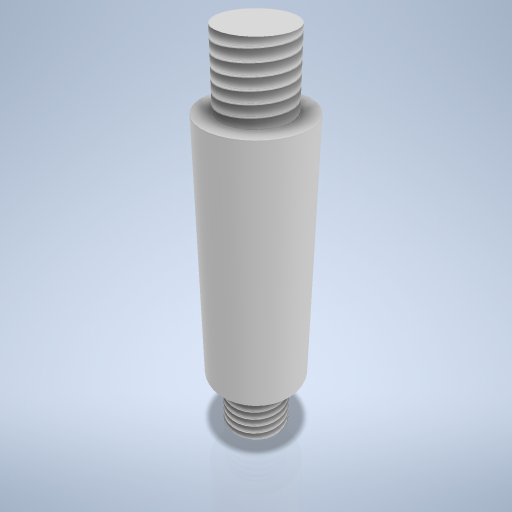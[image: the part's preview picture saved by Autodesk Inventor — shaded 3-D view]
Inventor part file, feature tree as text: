
AUTODESK INVENTOR PART (.ipt)
format: ipt  version: 2024.2 (Build 282272000, 272)  size: 269,824 bytes
history: native  units: mm
features: revolve x1, thread x1, sketch x1
ambient origin geometry x8: Origin, YZ Plane, XZ Plane, XY Plane, X Axis, Y Axis, Z Axis, Center Point
bodies: Volumenkörper1 (feature_tree)
feature tree (3):
  revolve  "Umdrehung1"
  thread  "Gewinde1"  [1 undecoded]
  sketch  "Skizze1"  dims[d1=10.0mm d2=40.0mm d3=10.0mm d4=15.0mm d5=90.0deg d6=60.0mm d7=0.0mm]
note: 1 required parameter value undecoded (feature->parameter linkage not recoverable at this tier; creation-order binding heuristic only, values carry confidence <= 0.55)
